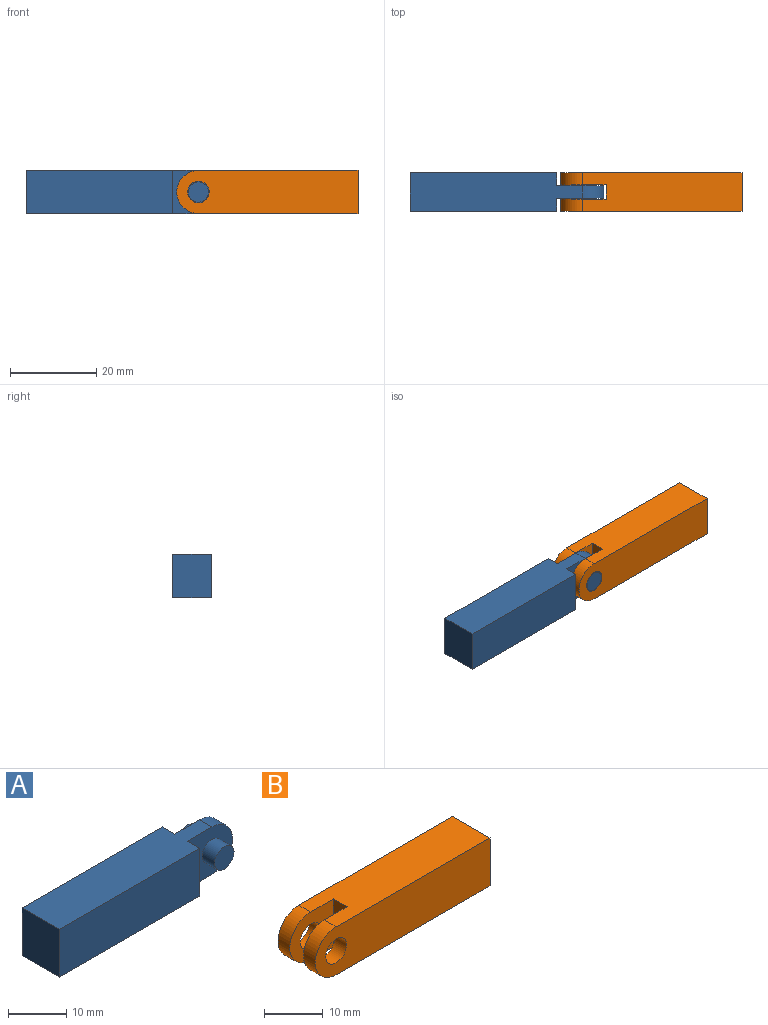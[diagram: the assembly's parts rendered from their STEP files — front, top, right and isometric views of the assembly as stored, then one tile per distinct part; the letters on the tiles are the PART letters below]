
ASSEMBLY  parts=2 mates=1
PART A: 14 faces, bbox 45x9x10 mm
  f0: plane 10x3mm, normal (1,0,0), area 30mm2, adj f1,f3,f6,f11
  f1: plane 40x9mm, normal (0,0,1), area 324mm2, adj f0,f2,f4,f5,f6,f9,f10,f11
  f2: plane 10x9mm, normal (-1,0,0), area 90mm2, adj f1,f3,f5,f6
  f3: plane 40x9mm, normal (0,0,-1), area 324mm2, adj f0,f2,f4,f5,f6,f9,f10,f11
  f4: plane 10x3mm, normal (1,0,0), area 30mm2, adj f1,f3,f5,f10
  f5: plane 34x10mm, normal (0,-1,0), area 340mm2, adj f1,f2,f3,f4
  f6: plane 34x10mm, normal (0,1,0), area 340mm2, adj f0,f1,f2,f3
  f7: cylinder r=2.35mm len=4.7mm, axis (0,1,0), area 44.3mm2, adj f8,f10
  f8: plane 4.7x4.7mm, normal (0,-1,0), area 17.3mm2, adj f7
  f9: cylinder r=5mm len=10mm, axis (0,1,0), area 47.1mm2, adj f1,f3,f10,f11
  f10: plane 11x10mm, normal (0,-1,0), area 81.9mm2, adj f1,f3,f4,f7,f9
  f11: plane 11x10mm, normal (0,1,0), area 81.9mm2, adj f0,f1,f3,f9,f13
  f12: plane 4.7x4.7mm, normal (0,1,0), area 17.3mm2, adj f13
  f13: cylinder r=2.35mm len=4.7mm, axis (0,1,0), area 44.3mm2, adj f11,f12
PART B: 12 faces, bbox 42x9x10 mm
  f0: plane 37.04x9mm, normal (0,0,1), area 315.2mm2, adj f1,f4,f5,f7,f8,f9,f10,f11
  f1: cylinder r=5mm len=10mm, axis (0,1,0), area 44.8mm2, adj f0,f2,f8,f10
  f2: plane 37.04x9mm, normal (0,0,-1), area 315.2mm2, adj f1,f4,f5,f7,f8,f9,f10,f11
  f3: cylinder r=2.5mm len=5mm, axis (0,1,0), area 44.8mm2, adj f8,f10
  f4: cylinder r=5mm len=10mm, axis (0,1,0), area 44.8mm2, adj f0,f2,f7,f9
  f5: plane 10x9mm, normal (1,0,0), area 90mm2, adj f0,f2,f7,f8
  f6: cylinder r=2.5mm len=5mm, axis (0,1,0), area 44.8mm2, adj f7,f9
  f7: plane 42.04x10mm, normal (0,-1,0), area 390mm2, adj f0,f2,f4,f5,f6
  f8: plane 42.04x10mm, normal (0,1,0), area 390mm2, adj f0,f1,f2,f3,f5
  f9: plane 10.5x10mm, normal (0,1,0), area 74.6mm2, adj f0,f2,f4,f6,f11
  f10: plane 10.5x10mm, normal (0,-1,0), area 74.6mm2, adj f0,f1,f2,f3,f11
  f11: plane 10x3.3mm, normal (-1,0,0), area 33mm2, adj f0,f2,f9,f10
PLACE A t=(-83.84,-1.01,84.09)mm
PLACE B t=(-32.76,-1.01,40.85)mm
MATE revolute A.f7 <-> B.f3  axis (0,-1,0) through (-32.76,-5.51,40.85)mm
